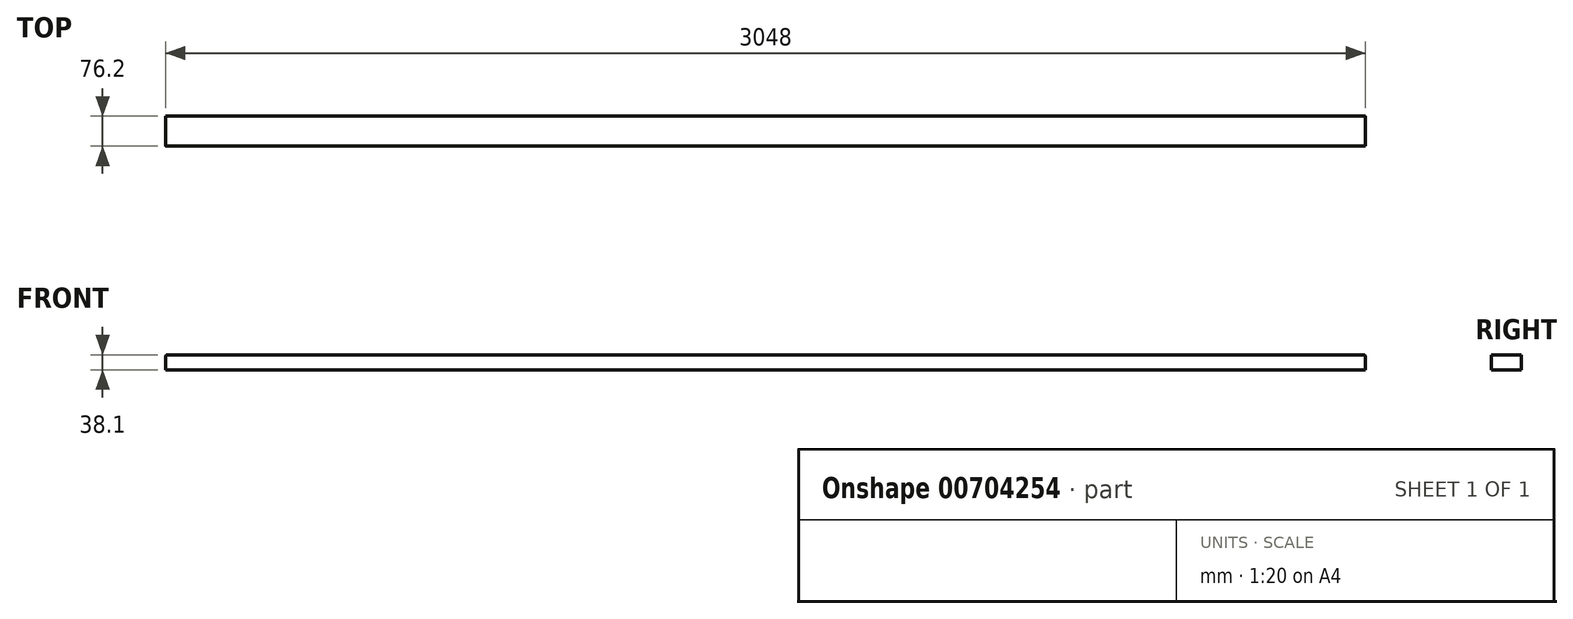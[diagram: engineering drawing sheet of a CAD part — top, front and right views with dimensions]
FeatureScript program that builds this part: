
annotation { "Feature Type Name" : "Feature", "Feature Type Description" : "" }
export const myFeature = defineFeature(function(context is Context, id is Id, definition is map)
    precondition{}
    {
        {
            var Q0;
            Q0=qCreatedBy(makeId("Front.planeOp"),FACE);
            var sketch = newSketch(context, id + "F0", { "sketchPlane" : qUnion([Q0])});
            skLineSegment(sketch, "E0.bottom", {"start": v(-1524, 19.05) * mm, "end": v(1524, 19.05) * mm});
            skLineSegment(sketch, "E0.top", {"start": v(-1524, -19.05) * mm, "end": v(1524, -19.05) * mm});
            skLineSegment(sketch, "E0.left", {"start": v(-1524, 19.05) * mm, "end": v(-1524, -19.05) * mm});
            skLineSegment(sketch, "E0.right", {"start": v(1524, 19.05) * mm, "end": v(1524, -19.05) * mm});
            skPoint(sketch, "E0.middle", {"position": v(0, 0) * mm});
            skSolve(sketch);
        }
        {
            var Q0;
            Q0=makeQuery(id+"F0.imprint","IMPRINT",FACE,{"disambiguationData":[TD([[makeQuery(id+"F0.imprint","IMPRINT",EDGE,{"derivedFrom":sQuery(id+"F0.wireOp",EDGE,"E0.bottom")}),-1.0]])]});
            extrude(context, id + "F1", {"entities" : qUnion([Q0]), "endBound" : BoundingType.SYMMETRIC, "depth" : 76.2 * mm, "offsetDistance" : 25.4 * mm});
        }
        {
            var Q0;
            Q0=makeQuery(id+"F1.opExtrude","SWEPT_EDGE",EDGE,{"disambiguationData":[OSD([sQuery(id+"F0.wireOp",EDGE,"E0.bottom"),sQuery(id+"F0.wireOp",EDGE,"E0.left")])]});
            var Q1;
            Q1=makeQuery(id+"F1.opExtrude","SWEPT_EDGE",EDGE,{"disambiguationData":[OSD([sQuery(id+"F0.wireOp",EDGE,"E0.bottom"),sQuery(id+"F0.wireOp",EDGE,"E0.right")])]});
            fillet(context, id + "F2", {"entities" : qUnion([Q0, Q1]), "radius" : 5.08 * mm, "tangentPropagation" : true, "allowEdgeOverflow" : false});
        }
    });
